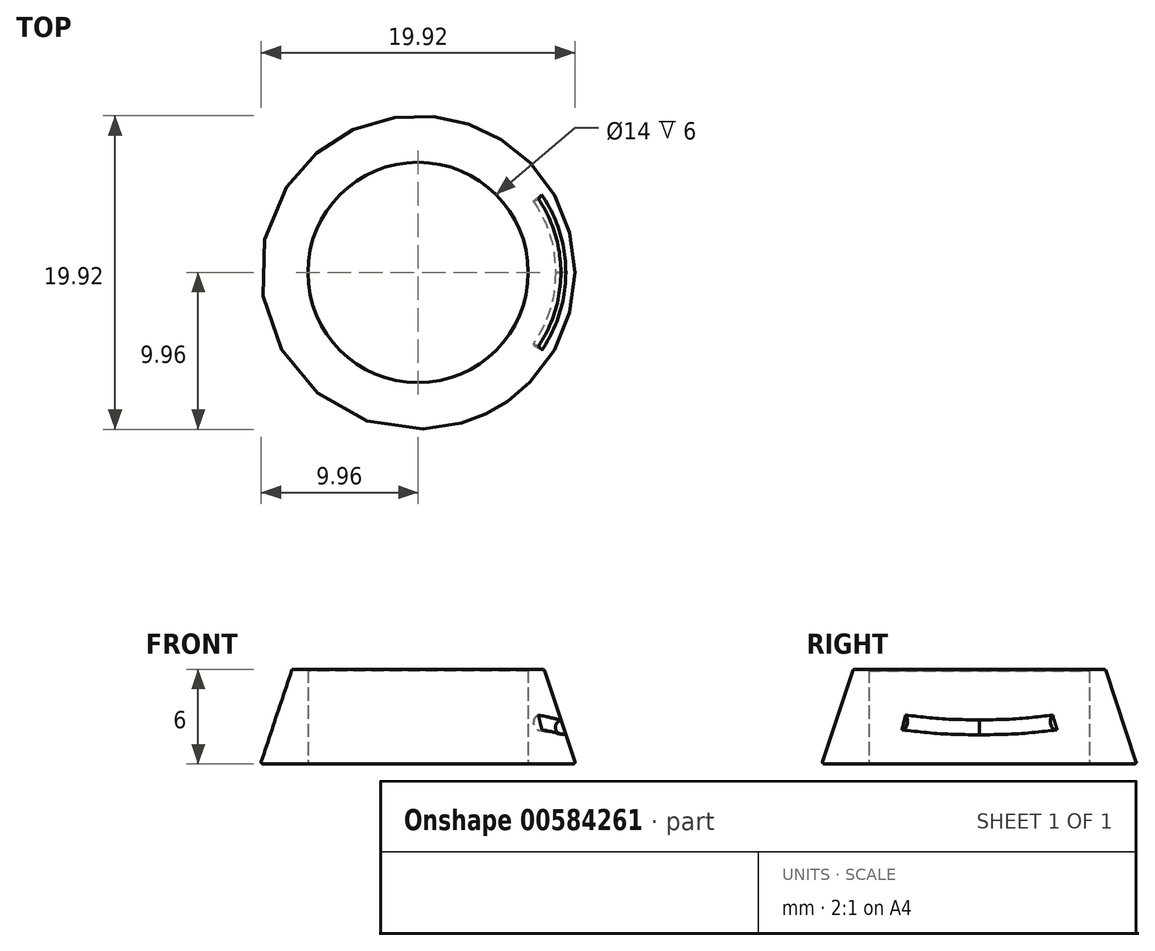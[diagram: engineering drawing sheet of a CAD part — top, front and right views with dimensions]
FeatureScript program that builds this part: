
annotation { "Feature Type Name" : "Feature", "Feature Type Description" : "" }
export const myFeature = defineFeature(function(context is Context, id is Id, definition is map)
    precondition{}
    {
        {
            var Q0;
            Q0=qCreatedBy(makeId("Top.planeOp"),FACE);
            var sketch = newSketch(context, id + "F0", { "sketchPlane" : qUnion([Q0])});
            skCircle(sketch, "E0", {"center": v(0, 0) * mm, "radius": 10 * mm});
            skCircle(sketch, "E1", {"center": v(0, 0) * mm, "radius": 8 * mm});
            skCircle(sketch, "E2", {"center": v(0, 0) * mm, "radius": 7 * mm});
            skPoint(sketch, "E3", {"position": v(20, 6.54) * mm});
            skPoint(sketch, "E4", {"position": v(20, -5.82) * mm});
            skSolve(sketch);
        }
        {
            var Q0;
            Q0=makeQuery(id+"F0.imprint","IMPRINT",FACE,{"disambiguationData":[TD([[makeQuery(id+"F0.imprint","IMPRINT",EDGE,{"derivedFrom":sQuery(id+"F0.wireOp",EDGE,"E1")}),1.0]])]});
            extrude(context, id + "F1", {"entities" : qUnion([Q0]), "depth" : 6 * mm, "offsetDistance" : 25 * mm});
        }
        {
            var Q0;
            Q0=makeQuery(id+"F0.imprint","IMPRINT",FACE,{"disambiguationData":[TD([[makeQuery(id+"F0.imprint","IMPRINT",EDGE,{"derivedFrom":sQuery(id+"F0.wireOp",EDGE,"E2")}),1.0]])]});
            extrude(context, id + "F2", {"entities" : qUnion([Q0]), "depth" : 5.9 * mm, "offsetDistance" : 25 * mm});
        }
        {
            var Q0;
            Q0=qCreatedBy(makeId("Front.planeOp"),FACE);
            var sketch = newSketch(context, id + "F3", { "sketchPlane" : qUnion([Q0])});
            skLineSegment(sketch, "E5", {"start": v(8, 6) * mm, "end": v(8, 0) * mm});
            skLineSegment(sketch, "E6", {"start": v(-8, 0) * mm, "end": v(-8, 6) * mm});
            skLineSegment(sketch, "E7.0", {"start": v(-10, 0) * mm, "end": v(10, 0) * mm});
            skLineSegment(sketch, "E8", {"start": v(-8, 6) * mm, "end": v(-10, 0) * mm});
            skSolve(sketch);
        }
        {
            var Q0;
            {var subQ0=sQuery(id+"F3.wireOp",EDGE,"E8");Q0=makeQuery(id+"F3.imprint","IMPRINT",FACE,{"disambiguationData":[TD([[makeQuery(id+"F3.imprint","IMPRINT",EDGE,{"derivedFrom":subQ0}),1.0]])]});}
            var Q1;
            Q1=makeQuery(id+"F1.opExtrude","SWEPT_FACE",FACE,{"disambiguationData":[OSD([sQuery(id+"F0.wireOp",EDGE,"E1")])]});
            revolve(context, id + "F4", {"operationType" : NewBodyOperationType.ADD, "entities" : qUnion([Q0]), "axis" : qUnion([Q1]), "revolveType" : RevolveType.FULL});
        }
        {
            var Q0;
            Q0=makeQuery(id+"F4.boolean.opBoolean","MERGE",EDGE,{"derivedFrom":[makeQuery(id+"F1.opExtrude","CAP_EDGE",EDGE,{"disambiguationData":[OSD([sQuery(id+"F0.wireOp",EDGE,"E1")])],"isStart":false}),makeQuery(id+"F4.opRevolve","SWEPT_EDGE",EDGE,{"disambiguationData":[OSD([sQuery(id+"F3.wireOp",EDGE,"E8"),sQuery(id+"F3.wireOp",EDGE,"E6")])]})]});
            var Q1;
            Q1=makeQuery(id+"F4.opRevolve","SWEPT_EDGE",EDGE,{"disambiguationData":[OSD([sQuery(id+"F3.wireOp",EDGE,"E7.0"),sQuery(id+"F3.wireOp",EDGE,"E8")])]});
            fillet(context, id + "F5", {"entities" : qUnion([Q0, Q1]), "radius" : 0.1 * mm, "tangentPropagation" : true, "allowEdgeOverflow" : false});
        }
        {
            var Q0;
            Q0=qCreatedBy(makeId("Top.planeOp"),FACE);
            cPlane(context, id + "F6", {"entities" : qUnion([Q0]), "cplaneType" : CPlaneType.OFFSET, "offset" : 6 * mm, "width" : 150 * mm, "height" : 150 * mm});
        }
        {
            var Q0;
            Q0=qCreatedBy(id+"F6.planeOp",FACE);
            var sketch = newSketch(context, id + "F7", { "sketchPlane" : qUnion([Q0])});
            skCircle(sketch, "E9.0", {"center": v(0, 0) * mm, "radius": 7.93 * mm});
            skPoint(sketch, "E10", {"position": v(-7.93, 0) * mm});
            skSolve(sketch);
        }
        {
            var Q0;
            Q0=sQuery(id+"F7.wireOp",VERTEX,"E10");
            var Q1;
            Q1=sQuery(id+"F0.wireOp",VERTEX,"E3");
            var Q2;
            Q2=sQuery(id+"F0.wireOp",VERTEX,"E4");
            cPlane(context, id + "F8", {"entities" : qUnion([Q0, Q1, Q2]), "cplaneType" : CPlaneType.THREE_POINT, "offset" : 25 * mm, "width" : 150 * mm, "height" : 150 * mm});
        }
        {
            var Q0;
            Q0=qCreatedBy(id+"F8.planeOp",FACE);
            var sketch = newSketch(context, id + "F9", { "sketchPlane" : qUnion([Q0])});
            skEllipticalArc(sketch, "E11", {});
            skFitSpline(sketch, "E12", {"points": [v(8.54, 0) * mm, v(8.42, 1.42) * mm, v(8.19, 2.39) * mm, v(7.74, 3.57) * mm, v(7.03, 4.8) * mm], "startDerivative": vector(-0.38, 5.67) * mm, "endDerivative": vector(-2.86, 4.6) * mm});
            skFitSpline(sketch, "E13.MirrorCS", {"points": [v(8.54, 0) * mm, v(8.42, -1.42) * mm, v(8.19, -2.39) * mm, v(7.74, -3.57) * mm, v(7.03, -4.8) * mm], "startDerivative": vector(-0.38, -5.67) * mm, "endDerivative": vector(-2.86, -4.6) * mm});
            const initialGuessF9  = {"E11": [-0.00027172453426008364, 0, 1, 0, 0.008808409505540248, 0.008589796045326137, 3.4419435747436085, 2.841241732435977]};
            skSetInitialGuess(sketch, initialGuessF9);
            skSolve(sketch);
        }
        {
            var Q0;
            Q0=qCreatedBy(makeId("Front.planeOp"),FACE);
            var sketch = newSketch(context, id + "F10", { "sketchPlane" : qUnion([Q0])});
            skLineSegment(sketch, "E14", {"start": v(9.96, 0.13) * mm, "end": v(8.02, 5.93) * mm});
            skLineSegment(sketch, "E15", {"start": v(-8.02, 5.93) * mm, "end": v(-9.96, 0.13) * mm});
            skLineSegment(sketch, "E16", {"start": v(5.32, 3.15) * mm, "end": v(8.35, 2.5) * mm});
            skFitSpline(sketch, "E17.0", {"points": [v(9.23, 2.31) * mm, v(9.2, 2.32) * mm, v(9.15, 2.33) * mm, v(8.9, 2.38) * mm, v(8.49, 2.47) * mm, v(8, 2.58) * mm, v(7.76, 2.63) * mm]});
            skCircle(sketch, "E18", {"center": v(9.23, 2.31) * mm, "radius": 0.5 * mm});
            skSolve(sketch);
        }
        {
            var Q0;
            {var subQ0=sQuery(id+"F10.wireOp",EDGE,"E17.0");var subQ1=sQuery(id+"F10.wireOp",EDGE,"E14");var subQ2=makeQuery(id+"F10.imprint","INTERSECT",VERTEX,{"derivedFrom":[subQ1,subQ0]});Q0=makeQuery(id+"F10.imprint","IMPRINT",FACE,{"disambiguationData":[TD([[makeQuery(id+"F10.imprint","IMPRINT",EDGE,{"disambiguationData":[TD([[subQ2,1.0]])],"derivedFrom":subQ1}),1.0]])]});}
            var Q1;
            {var subQ0=sQuery(id+"F10.wireOp",EDGE,"E17.0");var subQ1=sQuery(id+"F10.wireOp",EDGE,"E14");var subQ2=makeQuery(id+"F10.imprint","INTERSECT",VERTEX,{"derivedFrom":[subQ1,subQ0]});Q1=makeQuery(id+"F10.imprint","IMPRINT",FACE,{"disambiguationData":[TD([[makeQuery(id+"F10.imprint","IMPRINT",EDGE,{"disambiguationData":[TD([[subQ2,-1.0]])],"derivedFrom":subQ1}),1.0]])]});}
            var Q2;
            {var subQ0=sQuery(id+"F10.wireOp",EDGE,"E14");var subQ1=makeQuery(id+"F10.imprint","INTERSECT",VERTEX,{"derivedFrom":[subQ0,sQuery(id+"F10.wireOp",EDGE,"E17.0")]});Q2=makeQuery(id+"F10.imprint","IMPRINT",FACE,{"disambiguationData":[TD([[makeQuery(id+"F10.imprint","IMPRINT",EDGE,{"disambiguationData":[TD([[subQ1,1.0]])],"derivedFrom":subQ0}),-1.0]])]});}
            var Q3;
            Q3=sQuery(id+"F9.wireOp",EDGE,"E13.MirrorCS");
            var Q4;
            Q4=sQuery(id+"F9.wireOp",EDGE,"E12");
            sweep(context, id + "F11", {"operationType" : NewBodyOperationType.REMOVE, "profiles" : qUnion([Q0, Q1, Q2]), "path" : qUnion([Q3, Q4])});
        }
    });
